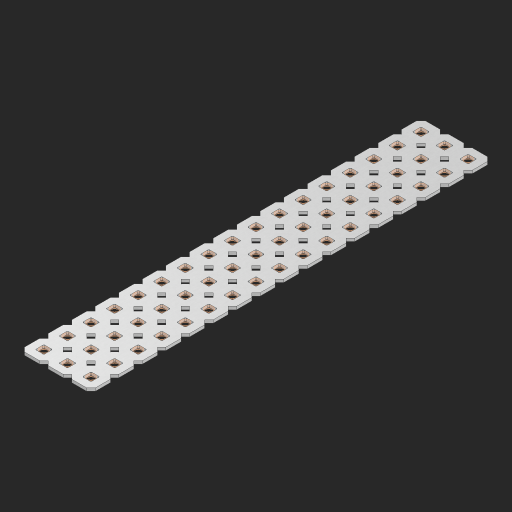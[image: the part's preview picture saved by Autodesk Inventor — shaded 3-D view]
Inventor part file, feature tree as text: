
AUTODESK INVENTOR PART (.ipt)
format: ipt  version: 2023 (Build 270158000, 158)  size: 866,304 bytes
history: native  units: in
note: dims shown in document units (in); Inventor stores cm internally (conversion verified against a paired STEP export)
features: other x52, extrude x50, sketch x2, pattern_linear x1
ambient origin geometry x8: Origin, YZ Plane, XZ Plane, XY Plane, X Axis, Y Axis, Z Axis, Center Point
bodies: Solid1 (feature_tree), Body (feature_tree)
feature tree (105):
  pattern_linear  "Rectangular Pattern1"  Spacing1=0.09in  [1 undecoded]
  sketch  "Sketch1"  dims[d1=0.5in]
  sketch  "Sketch2"  dims[d2=0.182in d3=0.09in d4=0.09in d5=0.09in d6=0.09in d7=0.09in d8=0.09in d9=0.09in d10=0.09in d11=0.02in d13=0.0in d14=0.172in d15=0.0625in d16=0.0in d19=0.5in d22=0.5in]
  other  "Srf1"
  other  "Srf126"
  other  "Srf127"
  other  "Srf128"
  other  "Srf129"
  other  "Srf130"
  other  "Srf131"
  other  "Srf250"
  other  "Srf251"
  other  "Srf252"
  other  "Srf253"
  other  "Srf254"
  other  "Srf255"
  other  "Srf256"
  other  "Srf257"
  other  "Srf258"
  other  "Srf259"
  other  "Srf268"
  other  "Srf269"
  other  "Srf270"
  other  "Srf271"
  other  "Srf272"
  other  "Srf273"
  other  "Srf274"
  other  "Srf275"
  other  "Srf276"
  other  "Srf277"
  other  "Srf278"
  other  "Srf279"
  other  "Srf280"
  other  "Srf281"
  other  "Srf282"
  other  "Srf283"
  other  "Srf284"
  other  "Srf293"
  other  "Srf294"
  other  "Srf295"
  other  "Srf296"
  other  "Srf297"
  other  "Srf298"
  other  "Srf299"
  other  "Srf300"
  other  "Srf301"
  other  "Srf302"
  other  "Srf303"
  other  "Srf304"
  other  "Srf305"
  other  "Srf306"
  other  "Srf307"
  other  "Srf308"
  other  "Srf309"
  other  "Circle"
  extrude  "ExtrusionSrf126"  Depth=0.09in
  extrude  "ExtrusionSrf127"  Depth=0.09in
  extrude  "ExtrusionSrf128"  Depth=0.09in
  extrude  "ExtrusionSrf129"  Depth=0.09in
  extrude  "ExtrusionSrf130"  Depth=0.09in
  extrude  "ExtrusionSrf131"  Depth=0.09in
  extrude  "ExtrusionSrf250"  Depth=0.09in
  extrude  "ExtrusionSrf251"  Depth=0.02in
  extrude  "ExtrusionSrf252"  TaperAngle=0.0deg  [1 undecoded]
  extrude  "ExtrusionSrf253"  Depth=0.5in
  extrude  "ExtrusionSrf254"  Depth=0.0625in TaperAngle=0.0deg
  extrude  "ExtrusionSrf255"  Depth=0.5in
  extrude  "ExtrusionSrf256"  Depth=0.5in
  extrude  "ExtrusionSrf257"  [1 undecoded]
  extrude  "ExtrusionSrf258"  [1 undecoded]
  extrude  "ExtrusionSrf259"  [1 undecoded]
  extrude  "ExtrusionSrf268"  [1 undecoded]
  extrude  "ExtrusionSrf269"  [1 undecoded]
  extrude  "ExtrusionSrf270"  [1 undecoded]
  extrude  "ExtrusionSrf271"  [1 undecoded]
  extrude  "ExtrusionSrf272"  [1 undecoded]
  extrude  "ExtrusionSrf273"  [1 undecoded]
  extrude  "ExtrusionSrf274"  [1 undecoded]
  extrude  "ExtrusionSrf275"  [1 undecoded]
  extrude  "ExtrusionSrf276"  [1 undecoded]
  extrude  "ExtrusionSrf277"  [1 undecoded]
  extrude  "ExtrusionSrf278"  [1 undecoded]
  extrude  "ExtrusionSrf279"  [1 undecoded]
  extrude  "ExtrusionSrf280"  [1 undecoded]
  extrude  "ExtrusionSrf281"  [1 undecoded]
  extrude  "ExtrusionSrf282"  [1 undecoded]
  extrude  "ExtrusionSrf283"  [1 undecoded]
  extrude  "ExtrusionSrf284"  [1 undecoded]
  extrude  "ExtrusionSrf293"  [1 undecoded]
  extrude  "ExtrusionSrf294"  [1 undecoded]
  extrude  "ExtrusionSrf295"  [1 undecoded]
  extrude  "ExtrusionSrf296"  [1 undecoded]
  extrude  "ExtrusionSrf297"  [1 undecoded]
  extrude  "ExtrusionSrf298"  [1 undecoded]
  extrude  "ExtrusionSrf299"  [1 undecoded]
  extrude  "ExtrusionSrf300"  [1 undecoded]
  extrude  "ExtrusionSrf301"  [1 undecoded]
  extrude  "ExtrusionSrf302"  [1 undecoded]
  extrude  "ExtrusionSrf303"  [1 undecoded]
  extrude  "ExtrusionSrf304"  [1 undecoded]
  extrude  "ExtrusionSrf305"  [1 undecoded]
  extrude  "ExtrusionSrf306"  [1 undecoded]
  extrude  "ExtrusionSrf307"  [1 undecoded]
  extrude  "ExtrusionSrf308"  [1 undecoded]
  extrude  "ExtrusionSrf309"  [1 undecoded]
note: 39 required parameter values undecoded (feature->parameter linkage not recoverable at this tier; creation-order binding heuristic only, values carry confidence <= 0.55)
